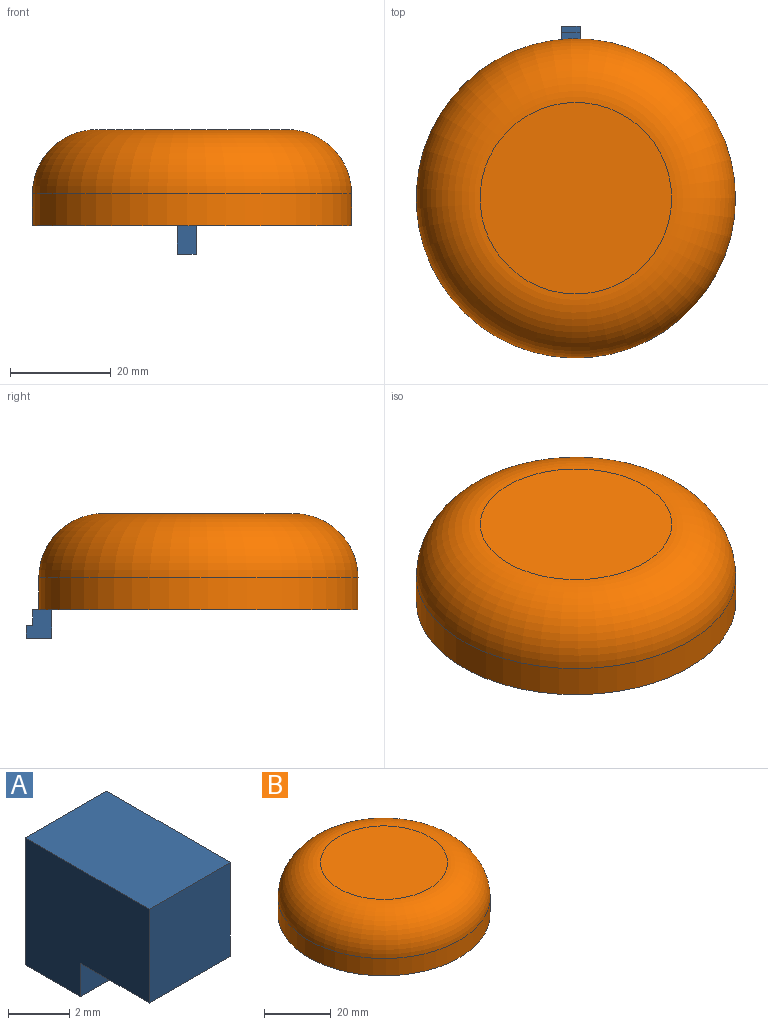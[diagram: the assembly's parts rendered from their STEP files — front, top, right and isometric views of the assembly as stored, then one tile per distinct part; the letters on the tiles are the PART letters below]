
ASSEMBLY  parts=2 mates=1
PART A: 8 faces, bbox 3.7x5.7x5.1 mm
  f0: plane 3.75x3.18mm, normal (0,0,-1), area 11.9mm2, adj f1,f5,f6,f7
  f1: plane 3.75x1.33mm, normal (0,-1,0), area 5mm2, adj f0,f2,f6,f7
  f2: plane 3.75x2.54mm, normal (0,0,-1), area 9.5mm2, adj f1,f3,f6,f7
  f3: plane 5.08x3.75mm, normal (0,1,0), area 19mm2, adj f2,f4,f6,f7
  f4: plane 5.72x3.75mm, normal (0,0,1), area 21.4mm2, adj f3,f5,f6,f7
  f5: plane 3.75x3.75mm, normal (0,-1,0), area 14mm2, adj f0,f4,f6,f7
  f6: plane 5.72x5.08mm, normal (1,0,0), area 24.8mm2, adj f0,f1,f2,f3,f4,f5
  f7: plane 5.72x5.08mm, normal (-1,0,0), area 24.8mm2, adj f0,f1,f2,f3,f4,f5
PART B: 35 faces, bbox 68.7x68.7x19.1 mm
  f0: plane 12.32x5.08mm, normal (1,0,0), area 62.6mm2, adj f2,f23,f25,f33
  f1: plane 12.32x5.08mm, normal (1,0,0), area 62.6mm2, adj f2,f14,f16,f29
  f2: plane 38.1x38.1mm, normal (0,0,-1), area 1088.5mm2, adj f0,f1,f8,f9,f10,f11,f12,f14
  f3: cylinder r=31.75mm len=63.5mm, axis (0,0,-1), area 1266.8mm2, adj f5,f6
  f4: plane 38.1x38.1mm, normal (0,0,1), area 1140.1mm2, adj f6
  f5: plane 63.5x63.5mm, normal (0,0,-1), area 486.4mm2, adj f3,f7
  f6: torus R=19.05mm, axis (0,0,1), area 3401.2mm2, adj f3,f4
  f7: cylinder r=29.21mm len=58.42mm, axis (0,0,-1), area 1165.4mm2, adj f5,f8
  f8: torus R=19.05mm, axis (0,0,1), area 2558.8mm2, adj f2,f7
  f9: plane 14.22x5.08mm, normal (1,0,0), area 72.3mm2, adj f2,f10,f12,f13
  f10: plane 14.22x3.18mm, normal (0,-1,0), area 37.3mm2, adj f2,f9,f11,f13,f27,f28
  f11: plane 12.32x5.08mm, normal (-1,0,0), area 62.6mm2, adj f2,f10,f12,f27
  f12: plane 14.22x3.18mm, normal (0,1,0), area 37.3mm2, adj f2,f9,f11,f13,f27,f28
  f13: plane 5.08x3.18mm, normal (0,0,-1), area 16.1mm2, adj f9,f10,f12,f28
  f14: plane 14.22x3.18mm, normal (0,-1,0), area 37.3mm2, adj f1,f2,f15,f17,f29,f30
  f15: plane 14.22x5.08mm, normal (-1,0,0), area 72.3mm2, adj f2,f14,f16,f17
  f16: plane 14.22x3.18mm, normal (0,1,0), area 37.3mm2, adj f1,f2,f15,f17,f29,f30
  f17: plane 5.08x3.18mm, normal (0,0,-1), area 16.1mm2, adj f14,f15,f16,f30
  f18: plane 14.22x3.18mm, normal (0,1,0), area 37.3mm2, adj f2,f19,f21,f22,f31,f32
  f19: plane 14.22x5.08mm, normal (1,0,0), area 72.3mm2, adj f2,f18,f20,f22
  f20: plane 14.22x3.18mm, normal (0,-1,0), area 37.3mm2, adj f2,f19,f21,f22,f31,f32
  f21: plane 12.32x5.08mm, normal (-1,0,0), area 62.6mm2, adj f2,f18,f20,f31
  f22: plane 5.08x3.18mm, normal (0,0,-1), area 16.1mm2, adj f18,f19,f20,f32
  f23: plane 14.22x3.18mm, normal (0,-1,0), area 37.3mm2, adj f0,f2,f24,f26,f33,f34
  f24: plane 14.22x5.08mm, normal (-1,0,0), area 72.3mm2, adj f2,f23,f25,f26
  f25: plane 14.22x3.18mm, normal (0,1,0), area 37.3mm2, adj f0,f2,f24,f26,f33,f34
  f26: plane 5.08x3.18mm, normal (0,0,-1), area 16.1mm2, adj f23,f24,f25,f34
  f27: plane 5.08x0.64mm, normal (0,0,1), area 3.2mm2, adj f10,f11,f12,f28
  f28: plane 5.08x1.91mm, normal (-1,0,0), area 9.7mm2, adj f10,f12,f13,f27
  f29: plane 5.08x0.64mm, normal (0,0,1), area 3.2mm2, adj f1,f14,f16,f30
  f30: plane 5.08x1.91mm, normal (1,0,0), area 9.7mm2, adj f14,f16,f17,f29
  f31: plane 5.08x0.64mm, normal (0,0,1), area 3.2mm2, adj f18,f20,f21,f32
  f32: plane 5.08x1.91mm, normal (-1,0,0), area 9.7mm2, adj f18,f20,f22,f31
  f33: plane 5.08x0.64mm, normal (0,0,1), area 3.2mm2, adj f0,f23,f25,f34
  f34: plane 5.08x1.91mm, normal (1,0,0), area 9.7mm2, adj f23,f25,f26,f33
PLACE A rot(axis=(0,0.71,-0.71),180deg) t=(-29.56,25.31,-4.84)mm
PLACE B t=(-30.42,-8.98,-1.67)mm
MATE planar A.f5 <-> B.f3  axis (0,0,1) through (-31.43,22.11,-1.67)mm
